# Revit family: 90000358 - Aventa Silent AVS100 - BIM file
name_source: partatom
category: Mechanical Equipment
units: mm (PartAtom-declared; Revit-internal decimal feet)

## family parameters
Always vertical = No
Classification = None
Cut with Voids When Loaded = No
Maintain Annotation Orientation = No
OmniClass Number = 23.75.35.17.11
OmniClass Title = Fans for Air Ductwork
Part Type = Breaks Into
Room Calculation Point = No
Round Connector Dimension = Use Diameter
Shared = No
Work Plane-Based = No

## types (2) — shared parameters
Current = 0 A
D = 100 mm  [stored 0.328084 ft]
D1 = 214 mm  [stored 0.7021 ft]
Dd12 = 3 mm  [stored 0.00984252 ft]
Dd13 = 4 mm  [stored 0.0131234 ft]
Dd14 = 39 mm  [stored 0.127953 ft]
Dd16 = 54 mm  [stored 0.177165 ft]
Dd22 = 3 mm  [stored 0.00984252 ft]
Dd23 = 4 mm  [stored 0.0131234 ft]
Dd24 = 39 mm  [stored 0.127953 ft]
Dd26 = 54 mm  [stored 0.177165 ft]
Description = In line mixed flow fan suitable for domestic and light commercial facilities
Dimensions = (H) 237 x (W) 505 x (D) 243mm
Distribution Box Material = Distribution Box Dark Grey
Duct Connection Size = 100 mm  [stored 0.328084 ft]
ElBoxH = 124 mm  [stored 0.406824 ft]
ElBoxL = 98 mm  [stored 0.321522 ft]
ElBoxR = 15 mm  [stored 0.0492126 ft]
ElBoxW = 116 mm  [stored 0.380577 ft]
Family Version = 1.0
Fan Material = Metal Black
Hanger Material = Metal Zinc
HangerBaseH = 113 mm  [stored 0.370735 ft]
HangerExtraL = Yes
HangerH = 113 mm  [stored 0.370735 ft]
HangerL = 208 mm
HangerL1 = 208 mm
HangerW = 93 mm  [stored 0.305118 ft]
L = 505 mm  [stored 1.65682 ft]
L1 = 25 mm  [stored 0.082021 ft]
L11 = 139 mm  [stored 0.456037 ft]
L12 = 8 mm  [stored 0.0262467 ft]
L13 = 13 mm
L14 = 34 mm
L15 = 70 mm
L16 = 8 mm  [stored 0.0262467 ft]
L17 = 6 mm  [stored 0.019685 ft]
L2 = 25 mm  [stored 0.082021 ft]
L21 = 184 mm  [stored 0.603675 ft]
L22 = 8 mm  [stored 0.0262467 ft]
L23 = 13 mm
L24 = 39 mm  [stored 0.127953 ft]
L25 = 110 mm
L26 = 8 mm  [stored 0.0262467 ft]
L27 = 6 mm  [stored 0.019685 ft]
Load Classification = HVAC
Maintenance Zone Height = 600 mm  [stored 1.9685 ft]
Maintenance Zone Length = 600 mm  [stored 1.9685 ft]
Maintenance Zone Length Calc = 600 mm  [stored 1.9685 ft]
Maintenance Zone Material = Maintenance Zone
Maintenance Zone Width = 600 mm  [stored 1.9685 ft]
Manufacturer = Airflow
Material Finish = Polymer Coated Steel
Model = Aventa Silent AVS100
Number of Poles = 1
Power Factor = 1
Protection rating = IPX4
R1 = 107 mm  [stored 0.35105 ft]
RPM (min-1) = 2630
Transported Air Temperature (°C) = -25...+60
URL = https://www.airflow.com
Voltage = 230 V
Weight = 4.60 kg
zero-valued in all types: Default Elevation

## per-type parameters (varying)
| type | Airflow part no | Apparent Power | Maximum Air Flow | Noise Level at 3 m (dBa) | Power | Type Comments |
| Aventa Silent AVS100 Timer | 90002118 | 26 VA | 240 m³/h | 29 | 26 W | Inline fan single speed up to 240m3/h |
| Aventa Silent AVS100 Basic | 90000358 | 24 VA | 170 m³/h | 24 | 24 W | Inline fan single speed up to 170m3/h |

note: [stored X ft] marks values corroborated as IEEE doubles in the binary element streams (Revit-internal decimal feet)

## geometry (parser evidence)
native form markers: Sweep x9
no freeform markers — native parametric forms only
